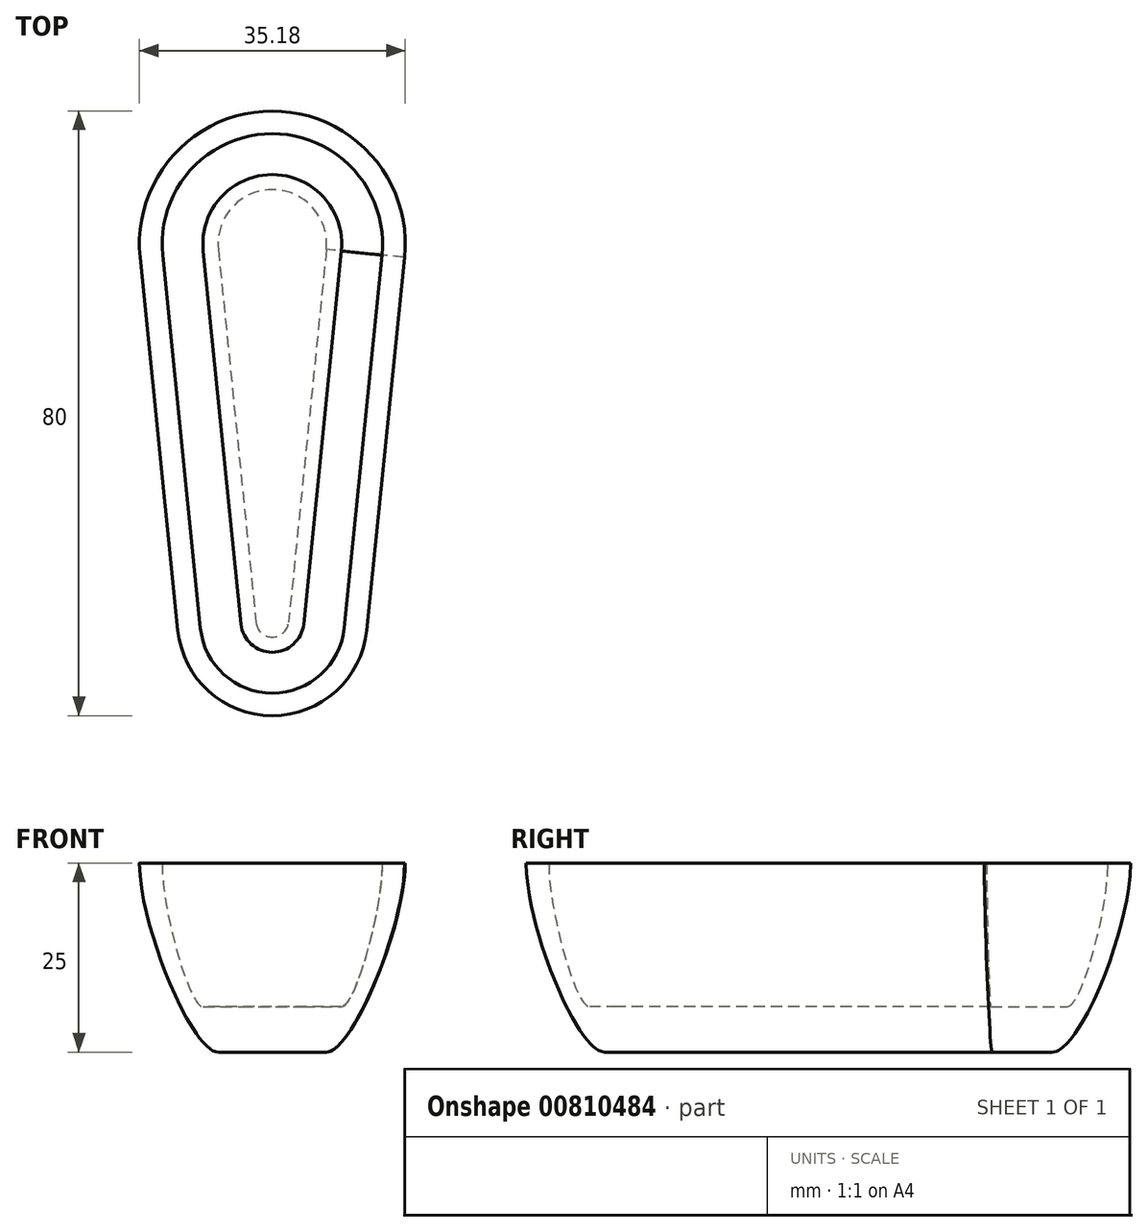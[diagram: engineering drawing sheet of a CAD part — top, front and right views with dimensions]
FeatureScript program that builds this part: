
annotation { "Feature Type Name" : "Feature", "Feature Type Description" : "" }
export const myFeature = defineFeature(function(context is Context, id is Id, definition is map)
    precondition{}
    {
        {
            var Q0;
            Q0=qCreatedBy(makeId("Top.planeOp"),FACE);
            var sketch = newSketch(context, id + "F0", { "sketchPlane" : qUnion([Q0])});
            skLineSegment(sketch, "E0", {"start": v(-17.5, 49.34) * mm, "end": v(17.5, 49.34) * mm, "construction": true});
            skArc(sketch, "E1", {"start": v(17.5, 49.34) * mm, "mid": v(0, 68.7) * mm, "end": v(-17.5, 49.34) * mm});
            skPoint(sketch, "E2", {"position": v(0, 68.7) * mm});
            skLineSegment(sketch, "E3", {"start": v(-12.5, 0) * mm, "end": v(12.5, 0) * mm, "construction": true});
            skArc(sketch, "E4", {"start": v(-12.5, 0) * mm, "mid": v(0, -11.3) * mm, "end": v(12.5, 0) * mm});
            skLineSegment(sketch, "E5", {"start": v(17.5, 49.34) * mm, "end": v(12.5, 0) * mm});
            skLineSegment(sketch, "E6", {"start": v(-17.5, 49.34) * mm, "end": v(-12.5, 0) * mm});
            skPoint(sketch, "E7", {"position": v(0, -11.3) * mm});
            skLineSegment(sketch, "E8.bottom", {"start": v(7.5, 35.43) * mm, "end": v(-7.5, 35.43) * mm, "construction": true});
            skLineSegment(sketch, "E8.top", {"start": v(7.5, 60.43) * mm, "end": v(-7.5, 60.43) * mm, "construction": true});
            skLineSegment(sketch, "E8.left", {"start": v(7.5, 35.43) * mm, "end": v(7.5, 60.43) * mm, "construction": true});
            skLineSegment(sketch, "E8.right", {"start": v(-7.5, 35.43) * mm, "end": v(-7.5, 60.43) * mm, "construction": true});
            skPoint(sketch, "E8.middle", {"position": v(0, 47.93) * mm});
            skPoint(sketch, "E9", {"position": v(0, 49.34) * mm});
            skArc(sketch, "E10.0", {"start": v(14.52, 49.64) * mm, "mid": v(0, 65.7) * mm, "end": v(-14.52, 49.64) * mm});
            skLineSegment(sketch, "E10.1", {"start": v(14.52, 49.64) * mm, "end": v(9.52, 0.3) * mm});
            skArc(sketch, "E10.2", {"start": v(-9.52, 0.3) * mm, "mid": v(0, -8.3) * mm, "end": v(9.52, 0.3) * mm});
            skLineSegment(sketch, "E10.3", {"start": v(-14.52, 49.64) * mm, "end": v(-9.52, 0.3) * mm});
            skSolve(sketch);
        }
        {
            var Q0;
            Q0=qCreatedBy(makeId("Top.planeOp"),FACE);
            cPlane(context, id + "F1", {"entities" : qUnion([Q0]), "cplaneType" : CPlaneType.OFFSET, "offset" : 25 * mm, "oppositeDirection" : true, "width" : 150 * mm, "height" : 150 * mm});
        }
        {
            var Q0;
            Q0=qCreatedBy(makeId("Top.planeOp"),FACE);
            var sketch = newSketch(context, id + "F2", { "sketchPlane" : qUnion([Q0])});
            skLineSegment(sketch, "E11.0", {"start": v(17.5, 49.34) * mm, "end": v(12.5, 0) * mm});
            skArc(sketch, "E12.0", {"start": v(17.5, 49.34) * mm, "mid": v(0, 68.7) * mm, "end": v(-17.5, 49.34) * mm});
            skLineSegment(sketch, "E13.0", {"start": v(-17.5, 49.34) * mm, "end": v(-12.5, 0) * mm});
            skArc(sketch, "E14.0", {"start": v(-12.5, 0) * mm, "mid": v(0, -11.3) * mm, "end": v(12.5, 0) * mm});
            skSolve(sketch);
        }
        {
            var Q0;
            Q0=qCreatedBy(id+"F1.planeOp",FACE);
            var sketch = newSketch(context, id + "F3", { "sketchPlane" : qUnion([Q0])});
            skArc(sketch, "E15.0", {"start": v(17.5, 49.34) * mm, "mid": v(0, 68.7) * mm, "end": v(-17.5, 49.34) * mm, "construction": true});
            skLineSegment(sketch, "E16.0", {"start": v(17.5, 49.34) * mm, "end": v(12.5, 0) * mm, "construction": true});
            skLineSegment(sketch, "E17.0", {"start": v(-17.5, 49.34) * mm, "end": v(-12.5, 0) * mm, "construction": true});
            skArc(sketch, "E18.0", {"start": v(-12.5, 0) * mm, "mid": v(0, -11.3) * mm, "end": v(12.5, 0) * mm, "construction": true});
            skArc(sketch, "E19.0", {"start": v(7.15, 50.39) * mm, "mid": v(0, 58.3) * mm, "end": v(-7.15, 50.39) * mm});
            skLineSegment(sketch, "E19.1", {"start": v(7.15, 50.39) * mm, "end": v(2.15, 1.05) * mm});
            skArc(sketch, "E19.2", {"start": v(-2.15, 1.05) * mm, "mid": v(0, -0.9) * mm, "end": v(2.15, 1.05) * mm});
            skLineSegment(sketch, "E19.3", {"start": v(-7.15, 50.39) * mm, "end": v(-2.15, 1.05) * mm});
            skSolve(sketch);
        }
        {
            var Q0;
            Q0 = qSketchRegion(id + "F2", true);
            var Q1;
            Q1 = qSketchRegion(id + "F3", true);
            loft(context, id + "F4", {"startCondition" : LoftEndDerivativeType.NORMAL_TO_PROFILE, "startMagnitude" : 1, "endCondition" : LoftEndDerivativeType.TANGENT_TO_PROFILE, "endMagnitude" : 1, "sheetProfilesArray" : [{ "sheetProfileEntities" : qUnion([Q0]) }, { "sheetProfileEntities" : qUnion([Q1]) }]});
        }
        {
            var Q0;
            Q0=qCreatedBy(makeId("Top.planeOp"),FACE);
            cPlane(context, id + "F5", {"entities" : qUnion([Q0]), "cplaneType" : CPlaneType.OFFSET, "offset" : 19 * mm, "oppositeDirection" : true, "width" : 150 * mm, "height" : 150 * mm});
        }
        {
            var Q0;
            Q0=qCreatedBy(makeId("Top.planeOp"),FACE);
            var sketch = newSketch(context, id + "F6", { "sketchPlane" : qUnion([Q0])});
            skLineSegment(sketch, "E20.0", {"start": v(14.52, 49.64) * mm, "end": v(9.52, 0.3) * mm});
            skArc(sketch, "E21.0", {"start": v(-9.52, 0.3) * mm, "mid": v(0, -8.3) * mm, "end": v(9.52, 0.3) * mm});
            skLineSegment(sketch, "E22.0", {"start": v(-14.52, 49.64) * mm, "end": v(-9.52, 0.3) * mm});
            skArc(sketch, "E23.0", {"start": v(14.52, 49.64) * mm, "mid": v(0, 65.7) * mm, "end": v(-14.52, 49.64) * mm});
            skSolve(sketch);
        }
        {
            var Q0;
            Q0=qCreatedBy(id+"F5.planeOp",FACE);
            var sketch = newSketch(context, id + "F7", { "sketchPlane" : qUnion([Q0])});
            skArc(sketch, "E24.0.0", {"start": v(7.15, 50.39) * mm, "mid": v(0, 58.3) * mm, "end": v(-7.15, 50.39) * mm, "construction": true});
            skLineSegment(sketch, "E24.0.1", {"start": v(-7.15, 50.39) * mm, "end": v(-2.15, 1.05) * mm, "construction": true});
            skArc(sketch, "E24.0.2", {"start": v(-2.15, 1.05) * mm, "mid": v(0, -0.9) * mm, "end": v(2.15, 1.05) * mm, "construction": true});
            skLineSegment(sketch, "E24.0.3", {"start": v(2.15, 1.05) * mm, "end": v(7.15, 50.39) * mm, "construction": true});
            skLineSegment(sketch, "E25.0", {"start": v(-9.14, 50.19) * mm, "end": v(-4.14, 0.85) * mm});
            skArc(sketch, "E25.1", {"start": v(9.14, 50.19) * mm, "mid": v(0, 60.3) * mm, "end": v(-9.14, 50.19) * mm});
            skLineSegment(sketch, "E25.2", {"start": v(4.14, 0.85) * mm, "end": v(9.14, 50.19) * mm});
            skArc(sketch, "E25.3", {"start": v(-4.14, 0.85) * mm, "mid": v(0, -2.9) * mm, "end": v(4.14, 0.85) * mm});
            skSolve(sketch);
        }
        {
            var Q0;
            Q0 = qSketchRegion(id + "F6", true);
            var Q1;
            Q1 = qSketchRegion(id + "F7", true);
            loft(context, id + "F8", {"startCondition" : LoftEndDerivativeType.NORMAL_TO_PROFILE, "startMagnitude" : 1, "endCondition" : LoftEndDerivativeType.TANGENT_TO_PROFILE, "endMagnitude" : 1, "sheetProfilesArray" : [{ "sheetProfileEntities" : qUnion([Q0]) }, { "sheetProfileEntities" : qUnion([Q1]) }]});
        }
        {
            var Q0;
            Q0=makeQuery(id+"F8.opLoft","SWEPT_BODY",BODY,{"disambiguationData":[OSD([makeQuery(id+"F6.imprint","IMPRINT",FACE,{"disambiguationData":[TD([[makeQuery(id+"F6.imprint","IMPRINT",EDGE,{"derivedFrom":sQuery(id+"F6.wireOp",EDGE,"E20.0")}),-1.0]])]}),makeQuery(id+"F7.imprint","IMPRINT",FACE,{"disambiguationData":[TD([[makeQuery(id+"F7.imprint","IMPRINT",EDGE,{"derivedFrom":sQuery(id+"F7.wireOp",EDGE,"E25.0")}),1.0]])]})])]});
            var Q1;
            Q1=makeQuery(id+"F4.opLoft","SWEPT_BODY",BODY,{"disambiguationData":[OSD([makeQuery(id+"F2.imprint","IMPRINT",FACE,{"disambiguationData":[TD([[makeQuery(id+"F2.imprint","IMPRINT",EDGE,{"derivedFrom":sQuery(id+"F2.wireOp",EDGE,"E11.0")}),-1.0]])]}),makeQuery(id+"F3.imprint","IMPRINT",FACE,{"disambiguationData":[TD([[makeQuery(id+"F3.imprint","IMPRINT",EDGE,{"derivedFrom":sQuery(id+"F3.wireOp",EDGE,"E19.0")}),1.0]])]})])]});
            booleanBodies(context, id + "F9", {"operationType" : BooleanOperationType.SUBTRACTION, "tools" : qUnion([Q0]), "targets" : qUnion([Q1])});
        }
    });
